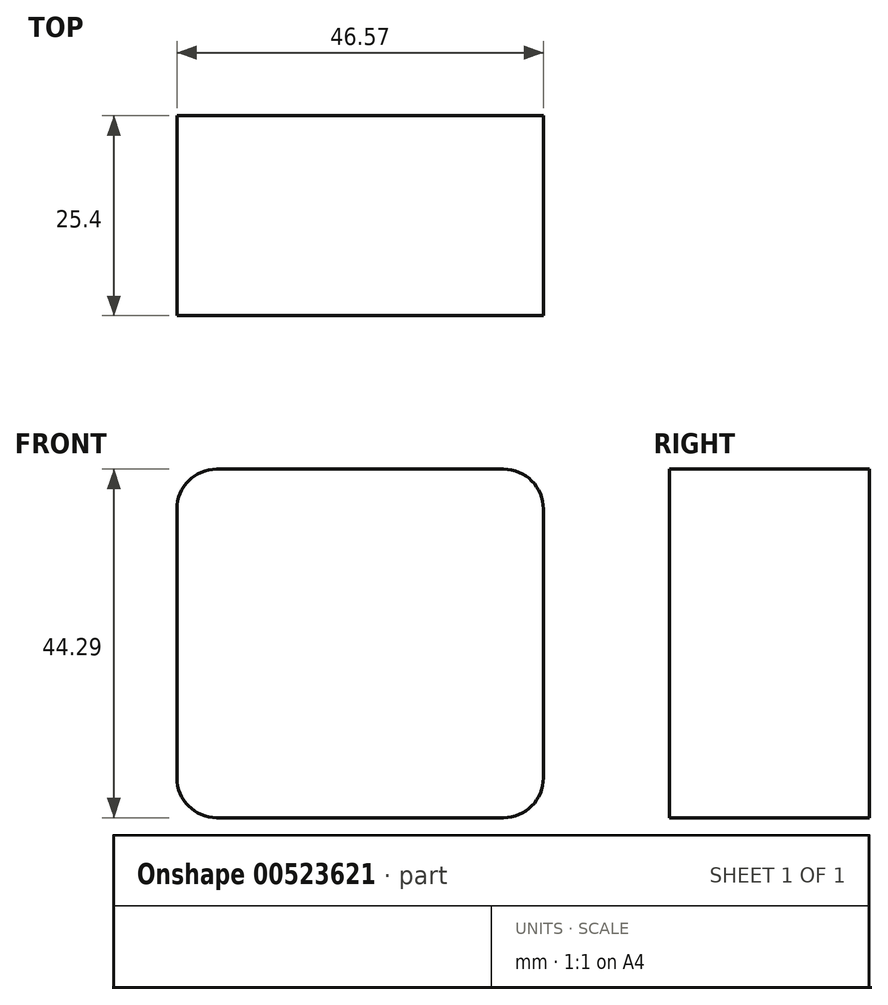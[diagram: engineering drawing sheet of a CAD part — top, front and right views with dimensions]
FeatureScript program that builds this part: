
annotation { "Feature Type Name" : "Feature", "Feature Type Description" : "" }
export const myFeature = defineFeature(function(context is Context, id is Id, definition is map)
    precondition{}
    {
        {
            var Q0;
            Q0=qCreatedBy(makeId("Front.planeOp"),FACE);
            var sketch = newSketch(context, id + "F0", { "sketchPlane" : qUnion([Q0])});
            skLineSegment(sketch, "E0.bottom", {"start": v(-26.05, 23.98) * mm, "end": v(20.52, 23.98) * mm});
            skLineSegment(sketch, "E0.top", {"start": v(-26.05, -20.3) * mm, "end": v(20.52, -20.3) * mm});
            skLineSegment(sketch, "E0.left", {"start": v(-26.05, 23.98) * mm, "end": v(-26.05, -20.3) * mm});
            skLineSegment(sketch, "E0.right", {"start": v(20.52, 23.98) * mm, "end": v(20.52, -20.3) * mm});
            skSolve(sketch);
        }
        {
            var Q0;
            Q0=makeQuery(id+"F0.imprint","IMPRINT",FACE,{"disambiguationData":[TD([[makeQuery(id+"F0.imprint","IMPRINT",EDGE,{"derivedFrom":sQuery(id+"F0.wireOp",EDGE,"E0.bottom")}),-1.0]])]});
            extrude(context, id + "F1", {"entities" : qUnion([Q0]), "depth" : 25.4 * mm, "offsetDistance" : 25.4 * mm});
        }
        {
            var Q0;
            Q0=makeQuery(id+"F1.opExtrude","SWEPT_EDGE",EDGE,{"disambiguationData":[OSD([sQuery(id+"F0.wireOp",EDGE,"E0.bottom"),sQuery(id+"F0.wireOp",EDGE,"E0.right")])]});
            var Q1;
            Q1=makeQuery(id+"F1.opExtrude","SWEPT_EDGE",EDGE,{"disambiguationData":[OSD([sQuery(id+"F0.wireOp",EDGE,"E0.bottom"),sQuery(id+"F0.wireOp",EDGE,"E0.left")])]});
            var Q2;
            Q2=makeQuery(id+"F1.opExtrude","SWEPT_EDGE",EDGE,{"disambiguationData":[OSD([sQuery(id+"F0.wireOp",EDGE,"E0.top"),sQuery(id+"F0.wireOp",EDGE,"E0.right")])]});
            var Q3;
            Q3=makeQuery(id+"F1.opExtrude","SWEPT_EDGE",EDGE,{"disambiguationData":[OSD([sQuery(id+"F0.wireOp",EDGE,"E0.top"),sQuery(id+"F0.wireOp",EDGE,"E0.left")])]});
            fillet(context, id + "F2", {"entities" : qUnion([Q0, Q1, Q2, Q3]), "radius" : 5.08 * mm, "tangentPropagation" : true, "allowEdgeOverflow" : false});
        }
    });
